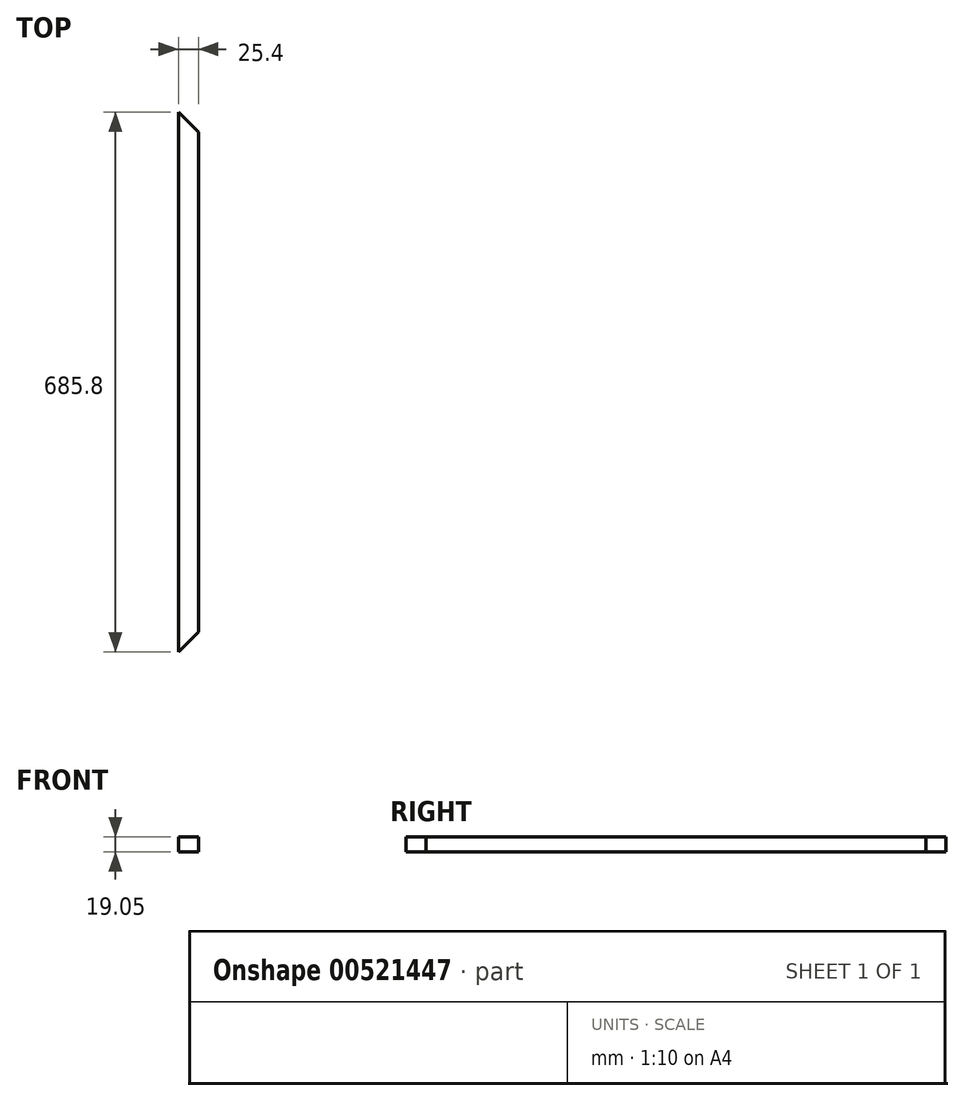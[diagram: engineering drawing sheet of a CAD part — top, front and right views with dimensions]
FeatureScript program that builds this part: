
annotation { "Feature Type Name" : "Feature", "Feature Type Description" : "" }
export const myFeature = defineFeature(function(context is Context, id is Id, definition is map)
    precondition{}
    {
        {
            var Q0;
            Q0=qCreatedBy(makeId("Top.planeOp"),FACE);
            var sketch = newSketch(context, id + "F0", { "sketchPlane" : qUnion([Q0])});
            skLineSegment(sketch, "E0.bottom", {"start": v(-16.38, 651.99) * mm, "end": v(9.02, 651.99) * mm});
            skLineSegment(sketch, "E0.top", {"start": v(-16.38, -33.81) * mm, "end": v(9.02, -33.81) * mm});
            skLineSegment(sketch, "E0.left", {"start": v(-16.38, 651.99) * mm, "end": v(-16.38, -33.81) * mm});
            skLineSegment(sketch, "E0.right", {"start": v(9.02, 651.99) * mm, "end": v(9.02, -33.81) * mm});
            skSolve(sketch);
        }
        {
            var Q0;
            Q0=makeQuery(id+"F0.imprint","IMPRINT",FACE,{"disambiguationData":[TD([[makeQuery(id+"F0.imprint","IMPRINT",EDGE,{"derivedFrom":sQuery(id+"F0.wireOp",EDGE,"E0.bottom")}),-1.0]])]});
            extrude(context, id + "F1", {"entities" : qUnion([Q0]), "depth" : 19.05 * mm, "offsetDistance" : 25.4 * mm});
        }
        {
            var Q0;
            Q0=makeQuery(id+"F1.opExtrude","SWEPT_EDGE",EDGE,{"disambiguationData":[OSD([sQuery(id+"F0.wireOp",EDGE,"E0.top"),sQuery(id+"F0.wireOp",EDGE,"E0.right")])]});
            var Q1;
            Q1=makeQuery(id+"F1.opExtrude","SWEPT_EDGE",EDGE,{"disambiguationData":[OSD([sQuery(id+"F0.wireOp",EDGE,"E0.bottom"),sQuery(id+"F0.wireOp",EDGE,"E0.right")])]});
            chamfer(context, id + "F2", {"entities" : qUnion([Q0, Q1]), "width" : 25.4 * mm, "tangentPropagation" : true});
        }
    });
